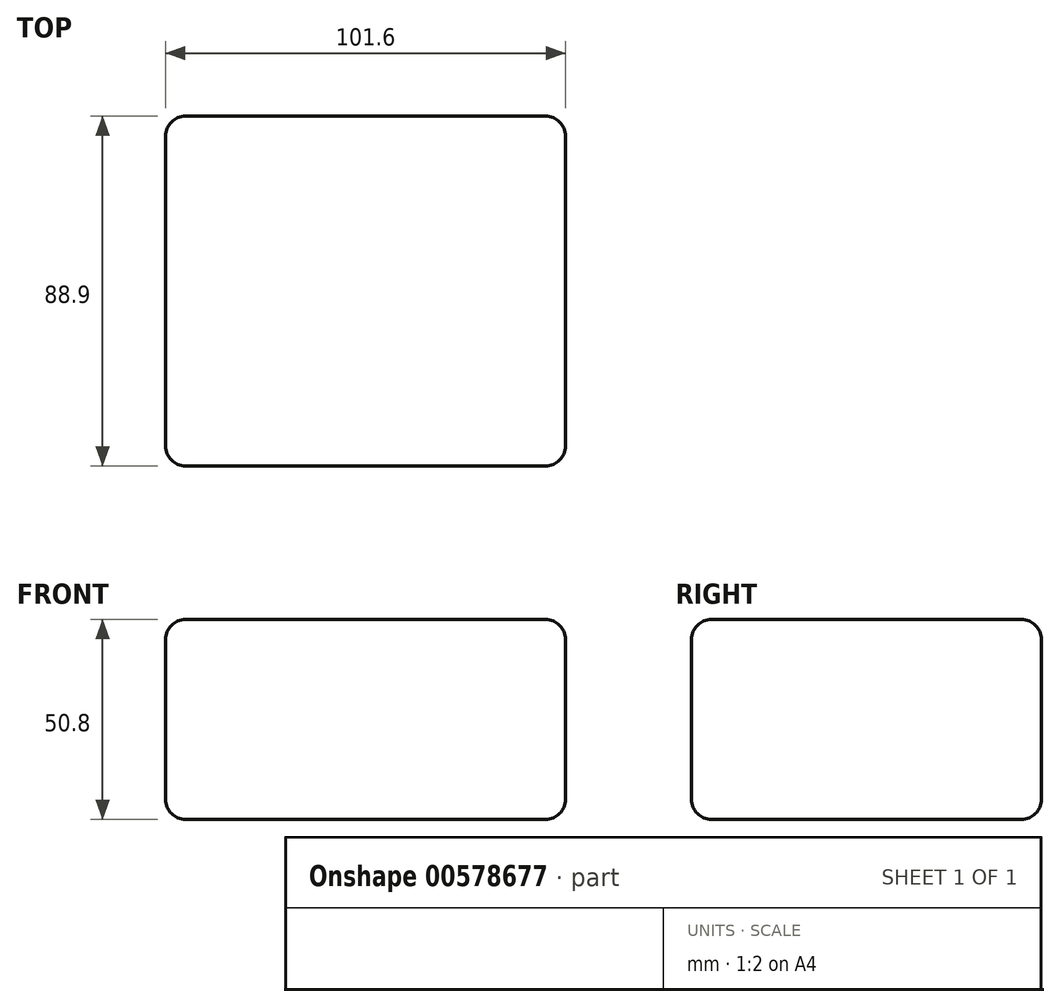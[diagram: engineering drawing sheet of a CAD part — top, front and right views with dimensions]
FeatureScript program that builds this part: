
annotation { "Feature Type Name" : "Feature", "Feature Type Description" : "" }
export const myFeature = defineFeature(function(context is Context, id is Id, definition is map)
    precondition{}
    {
        {
            var Q0;
            Q0=qCreatedBy(makeId("Top.planeOp"),FACE);
            var sketch = newSketch(context, id + "F0", { "sketchPlane" : qUnion([Q0])});
            skLineSegment(sketch, "E0.bottom", {"start": v(50.16, -23.91) * mm, "end": v(-51.44, -23.91) * mm});
            skLineSegment(sketch, "E0.top", {"start": v(50.16, 64.99) * mm, "end": v(-51.44, 64.99) * mm});
            skLineSegment(sketch, "E0.left", {"start": v(50.16, -23.91) * mm, "end": v(50.16, 64.99) * mm});
            skLineSegment(sketch, "E0.right", {"start": v(-51.44, -23.91) * mm, "end": v(-51.44, 64.99) * mm});
            skSolve(sketch);
        }
        {
            var Q0;
            Q0=makeQuery(id+"F0.imprint","IMPRINT",FACE,{"disambiguationData":[TD([[makeQuery(id+"F0.imprint","IMPRINT",EDGE,{"derivedFrom":sQuery(id+"F0.wireOp",EDGE,"E0.bottom")}),-1.0]])]});
            var Q1;
            Q1 = qSketchRegion(id + "F0", true);
            extrude(context, id + "F1", {"entities" : qUnion([Q0, Q1]), "depth" : 50.8 * mm, "offsetDistance" : 25.4 * mm});
        }
        {
            var Q0;
            Q0=makeQuery(id+"F1.opExtrude","CAP_FACE",FACE,{"disambiguationData":[OSD([sQuery(id+"F0.wireOp",EDGE,"E0.bottom"),sQuery(id+"F0.wireOp",EDGE,"E0.top"),sQuery(id+"F0.wireOp",EDGE,"E0.left"),sQuery(id+"F0.wireOp",EDGE,"E0.right")])],"isStart":false});
            var Q1;
            Q1=makeQuery(id+"F1.opExtrude","SWEPT_FACE",FACE,{"disambiguationData":[OSD([sQuery(id+"F0.wireOp",EDGE,"E0.bottom")])]});
            var Q2;
            Q2=makeQuery(id+"F1.opExtrude","SWEPT_FACE",FACE,{"disambiguationData":[OSD([sQuery(id+"F0.wireOp",EDGE,"E0.left")])]});
            var Q3;
            Q3=makeQuery(id+"F1.opExtrude","SWEPT_FACE",FACE,{"disambiguationData":[OSD([sQuery(id+"F0.wireOp",EDGE,"E0.top")])]});
            var Q4;
            Q4=makeQuery(id+"F1.opExtrude","CAP_FACE",FACE,{"disambiguationData":[OSD([sQuery(id+"F0.wireOp",EDGE,"E0.bottom"),sQuery(id+"F0.wireOp",EDGE,"E0.top"),sQuery(id+"F0.wireOp",EDGE,"E0.left"),sQuery(id+"F0.wireOp",EDGE,"E0.right")])],"isStart":true});
            fillet(context, id + "F2", {"entities" : qUnion([Q0, Q1, Q2, Q3, Q4]), "radius" : 5.08 * mm, "tangentPropagation" : true, "allowEdgeOverflow" : false});
        }
    });
